# Revit family: NaughtOne_Symbol90DegreeCurveWork
name_source: partatom
category: Furniture
units: mm (PartAtom-declared; Revit-internal decimal feet)

## family parameters
Always vertical = Yes
Cut with Voids When Loaded = No
Enable Cutting in Views = No
OmniClass Number = 23.40.20.00
OmniClass Title = General Furniture and Specialties
Render Appearance Source = Family Geometry
Room Calculation Point = No
Shared = Yes
Work Plane-Based = No

## types (3) — shared parameters
Assembly Code = E2020200
Manufacturer = Herman Miller, Inc.
Package Qty = 1
URL = http://www.hermanmiller.com
zero-valued in all types: Default Elevation

## per-type parameters (varying)
| type | Curve Bench | Curve Seat | Description | Model | Type |
| Curve Bench Single Fabric Work Ht | Yes | No | Symbol 90 Degree Curve Bench Work height 18 inch seat height Single Fabric | NOSYN410W1 | 1 |
| Curve Seat Single Fabric Work Ht | No | Yes | Symbol 90 Degree Curve Seat Work height 18 inch seat height Single Fabric | NOSYN420W1 | 2 |
| Curve Seat Multiple Fabric Work Ht | No | Yes | Symbol 90 Degree Curve Seat Work height 18 inch seat height Multiple Fabric | NOSYN420W2 | 3 |

## geometry (parser evidence)
native form markers: Sweep x5
no freeform markers — native parametric forms only
